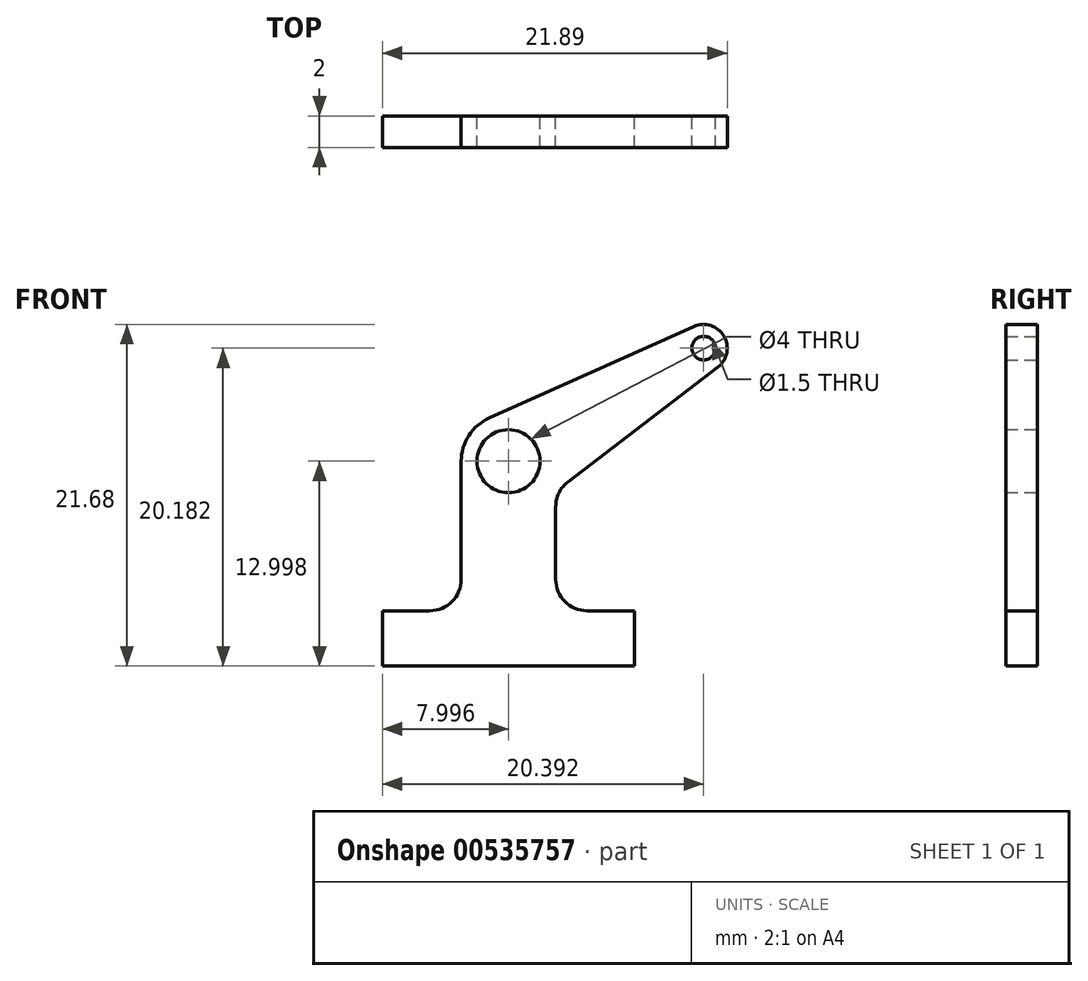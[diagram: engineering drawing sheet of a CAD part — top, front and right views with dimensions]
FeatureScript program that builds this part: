
annotation { "Feature Type Name" : "Feature", "Feature Type Description" : "" }
export const myFeature = defineFeature(function(context is Context, id is Id, definition is map)
    precondition{}
    {
        {
            var Q0;
            Q0=qCreatedBy(makeId("Front.planeOp"),FACE);
            var sketch = newSketch(context, id + "F0", { "sketchPlane" : qUnion([Q0])});
            skCircle(sketch, "E0", {"center": v(54.9, 6.96) * mm, "radius": 2 * mm});
            skArc(sketch, "E1", {"start": v(53.67, 9.7) * mm, "mid": v(52.38, 8.6) * mm, "end": v(51.9, 6.96) * mm});
            skArc(sketch, "E2", {"start": v(68.2, 12.95) * mm, "mid": v(68.58, 14.9) * mm, "end": v(66.68, 15.51) * mm});
            skCircle(sketch, "E3", {"center": v(67.3, 14.14) * mm, "radius": 0.75 * mm});
            skLineSegment(sketch, "E4", {"start": v(46.9, -6.04) * mm, "end": v(62.9, -6.04) * mm});
            skLineSegment(sketch, "E5", {"start": v(62.9, -6.04) * mm, "end": v(62.9, -2.54) * mm});
            skLineSegment(sketch, "E6", {"start": v(49.9, -2.54) * mm, "end": v(46.9, -2.54) * mm});
            skLineSegment(sketch, "E7", {"start": v(46.9, -2.54) * mm, "end": v(46.9, -6.04) * mm});
            skLineSegment(sketch, "E8", {"start": v(51.9, -0.54) * mm, "end": v(51.9, 6.96) * mm});
            skLineSegment(sketch, "E9", {"start": v(57.9, 4.07) * mm, "end": v(57.9, -0.54) * mm});
            skArc(sketch, "E10.filletArc", {"start": v(49.9, -2.54) * mm, "mid": v(51.31, -1.96) * mm, "end": v(51.9, -0.54) * mm});
            skLineSegment(sketch, "E11", {"start": v(62.9, -2.54) * mm, "end": v(59.9, -2.54) * mm});
            skPoint(sketch, "E12.visualSharp", {"position": v(57.9, -2.54) * mm});
            skArc(sketch, "E12.filletArc", {"start": v(57.9, -0.54) * mm, "mid": v(58.48, -1.96) * mm, "end": v(59.9, -2.54) * mm});
            skLineSegment(sketch, "E13", {"start": v(58.68, 5.66) * mm, "end": v(68.2, 12.95) * mm});
            skLineSegment(sketch, "E14", {"start": v(66.68, 15.51) * mm, "end": v(53.67, 9.7) * mm});
            skArc(sketch, "E15.filletArc", {"start": v(58.68, 5.66) * mm, "mid": v(58.1, 4.95) * mm, "end": v(57.9, 4.07) * mm});
            skSolve(sketch);
        }
        {
            var Q0;
            Q0 = qSketchRegion(id + "F0", true);
            extrude(context, id + "F1", {"entities" : qUnion([Q0]), "depth" : 2 * mm, "offsetDistance" : 25 * mm});
        }
    });
